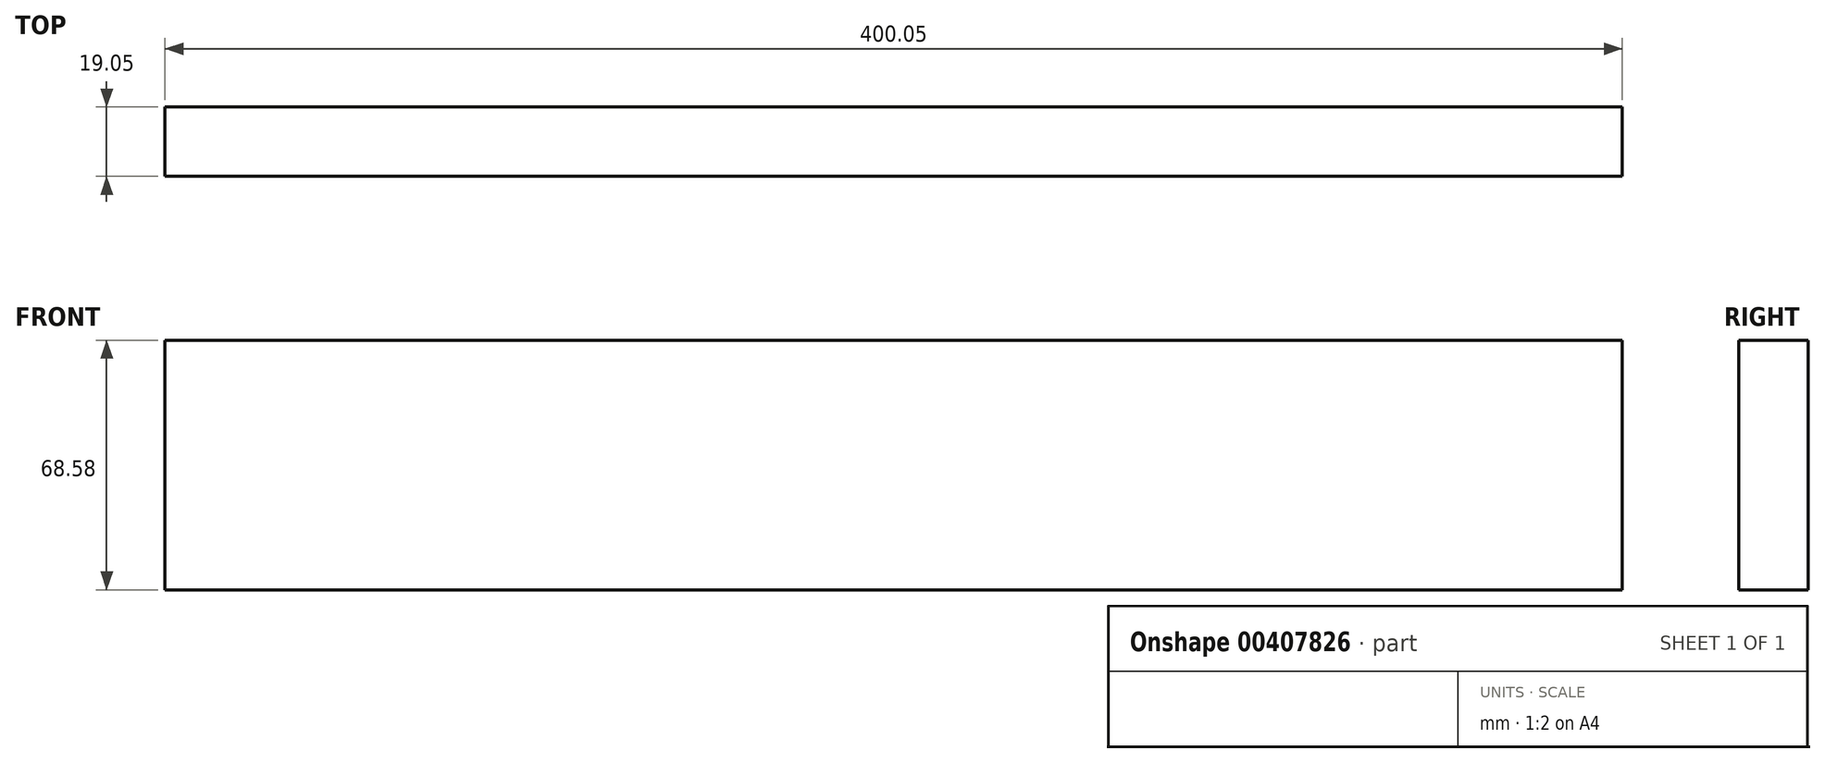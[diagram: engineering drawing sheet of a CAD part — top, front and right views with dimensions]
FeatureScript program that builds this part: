
annotation { "Feature Type Name" : "Feature", "Feature Type Description" : "" }
export const myFeature = defineFeature(function(context is Context, id is Id, definition is map)
    precondition{}
    {
        {
            var Q0;
            Q0=qCreatedBy(makeId("Front.planeOp"),FACE);
            var sketch = newSketch(context, id + "F0", { "sketchPlane" : qUnion([Q0])});
            skLineSegment(sketch, "E0.bottom", {"start": v(-191.65, 20.75) * mm, "end": v(208.4, 20.75) * mm});
            skLineSegment(sketch, "E0.top", {"start": v(-191.65, -47.83) * mm, "end": v(208.4, -47.83) * mm});
            skLineSegment(sketch, "E0.left", {"start": v(-191.65, 20.75) * mm, "end": v(-191.65, -47.83) * mm});
            skLineSegment(sketch, "E0.right", {"start": v(208.4, 20.75) * mm, "end": v(208.4, -47.83) * mm});
            skSolve(sketch);
        }
        {
            var Q0;
            Q0=makeQuery(id+"F0.imprint","IMPRINT",FACE,{"disambiguationData":[TD([[makeQuery(id+"F0.imprint","IMPRINT",EDGE,{"derivedFrom":sQuery(id+"F0.wireOp",EDGE,"E0.bottom")}),-1.0]])]});
            extrude(context, id + "F1", {"entities" : qUnion([Q0]), "depth" : 19.05 * mm});
        }
    });
